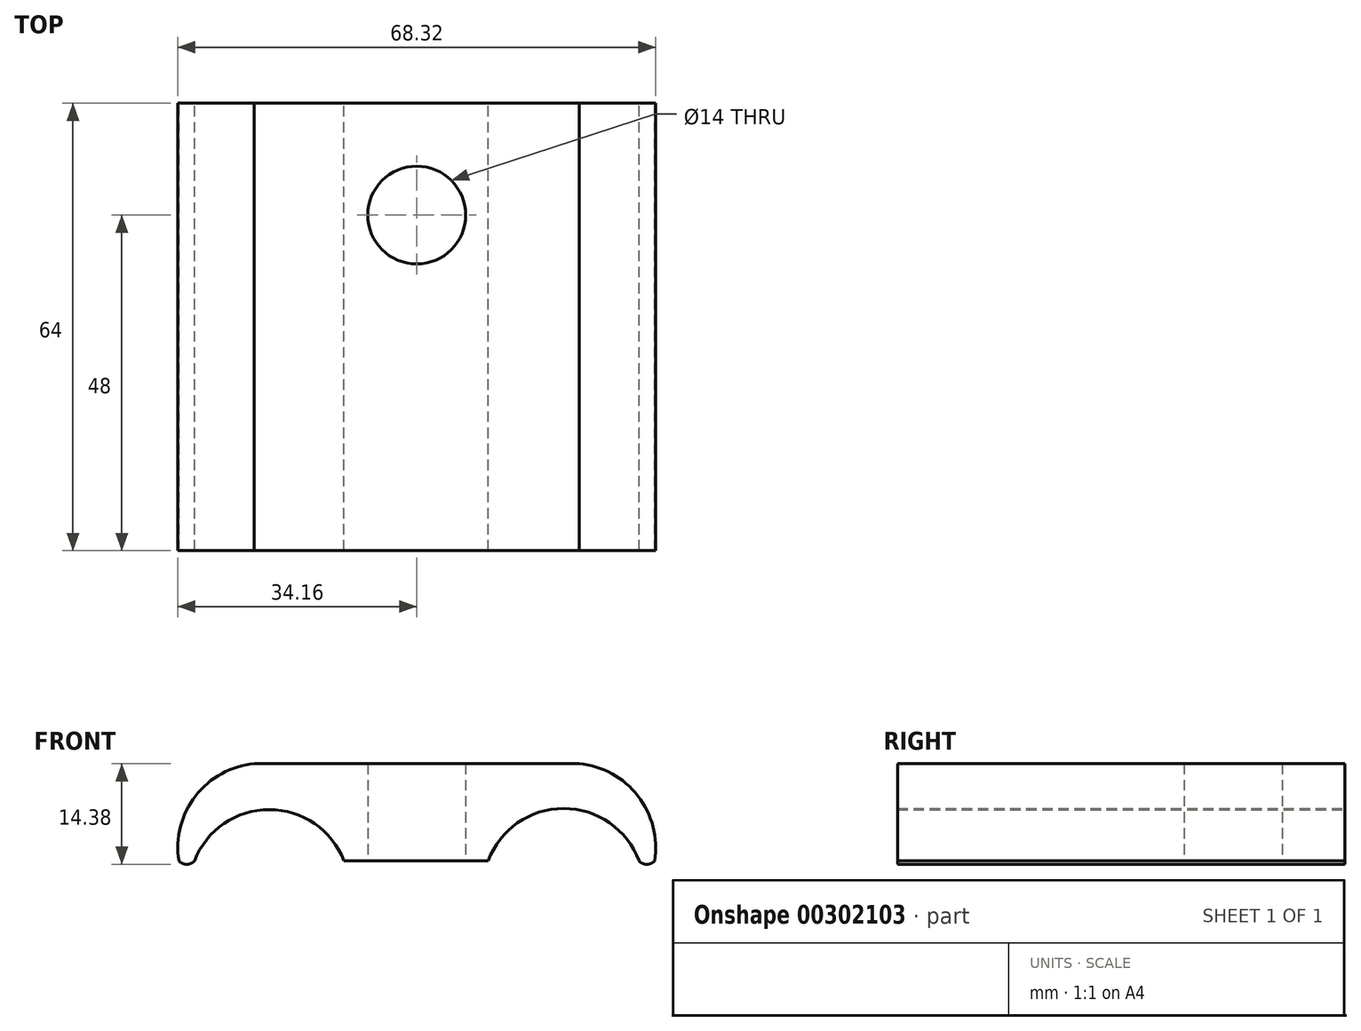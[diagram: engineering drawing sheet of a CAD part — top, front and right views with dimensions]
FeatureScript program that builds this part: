
annotation { "Feature Type Name" : "Feature", "Feature Type Description" : "" }
export const myFeature = defineFeature(function(context is Context, id is Id, definition is map)
    precondition{}
    {
        {
            var Q0;
            Q0=qCreatedBy(makeId("Front.planeOp"),FACE);
            var sketch = newSketch(context, id + "F0", { "sketchPlane" : qUnion([Q0])});
            skLineSegment(sketch, "E0", {"start": v(-34, 0) * mm, "end": v(-44.42, 0) * mm});
            skLineSegment(sketch, "E1", {"start": v(-34, 0) * mm, "end": v(-23.78, 0) * mm});
            skArc(sketch, "E2", {"start": v(-44.42, 0) * mm, "mid": v(-55.1, 7.34) * mm, "end": v(-65.78, 0) * mm});
            skArc(sketch, "E3", {"start": v(-2.22, 0) * mm, "mid": v(-13, 7.5) * mm, "end": v(-23.78, 0) * mm});
            skLineSegment(sketch, "E4", {"start": v(-13, 13.9) * mm, "end": v(-57.22, 13.9) * mm});
            skLineSegment(sketch, "E5", {"start": v(-13, 13.9) * mm, "end": v(-10.78, 13.9) * mm});
            skLineSegment(sketch, "E6", {"start": v(0, -0.1) * mm, "end": v(0, 0) * mm});
            skPoint(sketch, "E7.newPointB", {"position": v(0, 0) * mm});
            skPoint(sketch, "E8.start.orphan", {"position": v(-68, 0) * mm});
            skPoint(sketch, "E9.start.orphan", {"position": v(-65.78, 0) * mm});
            skArc(sketch, "E10", {"start": v(-55.1, 13.9) * mm, "mid": v(-64.95, 10.1) * mm, "end": v(-68, 0) * mm});
            skArc(sketch, "E11.MirrorCS", {"start": v(-12.9, 13.9) * mm, "mid": v(-4.48, 11.42) * mm, "end": v(0, 3.88) * mm});
            skPoint(sketch, "E12.orphan", {"position": v(0, 13.9) * mm});
            skPoint(sketch, "E13.orphan", {"position": v(-68, 13.9) * mm});
            skPoint(sketch, "E14.start.orphan", {"position": v(-68, 2.22) * mm});
            skArc(sketch, "E15", {"start": v(-68, 0) * mm, "mid": v(-66.9, -0.5) * mm, "end": v(-65.78, 0) * mm});
            skArc(sketch, "E16.MirrorCS", {"start": v(0, 0) * mm, "mid": v(-1.1, -0.5) * mm, "end": v(-2.22, 0) * mm});
            skArc(sketch, "E17.MirrorCS", {"start": v(-12.9, 13.9) * mm, "mid": v(-3.05, 10.1) * mm, "end": v(0, 0) * mm});
            skSolve(sketch);
        }
        {
            var Q0;
            Q0=makeQuery(id+"F0.imprint","IMPRINT",FACE,{"disambiguationData":[TD([[makeQuery(id+"F0.imprint","IMPRINT",EDGE,{"derivedFrom":sQuery(id+"F0.wireOp",EDGE,"E0")}),-1.0]])]});
            extrude(context, id + "F1", {"entities" : qUnion([Q0]), "depth" : 64 * mm});
        }
        {
            var Q0;
            Q0=qCreatedBy(makeId("Top.planeOp"),FACE);
            var sketch = newSketch(context, id + "F2", { "sketchPlane" : qUnion([Q0])});
            skLineSegment(sketch, "E18", {"start": v(0, 0) * mm, "end": v(-68, 0) * mm});
            skLineSegment(sketch, "E19", {"start": v(0, 0) * mm, "end": v(0, -64) * mm});
            skLineSegment(sketch, "E20", {"start": v(0, -32) * mm, "end": v(-34, -32) * mm});
            skPoint(sketch, "E20.endSnap0", {"position": v(-34, 0) * mm});
            skLineSegment(sketch, "E21", {"start": v(-34, -32) * mm, "end": v(-34, 0) * mm});
            skCircle(sketch, "E22", {"center": v(-34, -16) * mm, "radius": 7 * mm});
            skCircle(sketch, "E23.MirrorC", {"center": v(-34, -48) * mm, "radius": 7 * mm});
            skSolve(sketch);
        }
        {
            var Q0;
            Q0=makeQuery(id+"F2.imprint","IMPRINT",FACE,{"disambiguationData":[TD([[makeQuery(id+"F2.imprint","IMPRINT",EDGE,{"derivedFrom":sQuery(id+"F2.wireOp",EDGE,"E23.MirrorC")}),-1.0]])]});
            var Q1;
            {var subQ0=sQuery(id+"F2.wireOp",EDGE,"E22");var subQ1=sQuery(id+"F2.wireOp",EDGE,"E21");var subQ2=makeQuery(id+"F2.imprint","INTERSECT",VERTEX,{"disambiguationData":[OD(0.0)],"derivedFrom":[subQ1,subQ0]});Q1=makeQuery(id+"F2.imprint","IMPRINT",FACE,{"disambiguationData":[TD([[makeQuery(id+"F2.imprint","IMPRINT",EDGE,{"disambiguationData":[TD([[subQ2,-1.0]])],"derivedFrom":subQ1}),-1.0]])]});}
            var Q2;
            {var subQ0=sQuery(id+"F2.wireOp",EDGE,"E22");var subQ1=sQuery(id+"F2.wireOp",EDGE,"E21");var subQ2=makeQuery(id+"F2.imprint","INTERSECT",VERTEX,{"disambiguationData":[OD(0.0)],"derivedFrom":[subQ1,subQ0]});Q2=makeQuery(id+"F2.imprint","IMPRINT",FACE,{"disambiguationData":[TD([[makeQuery(id+"F2.imprint","IMPRINT",EDGE,{"disambiguationData":[TD([[subQ2,-1.0]])],"derivedFrom":subQ1}),1.0]])]});}
            var Q3;
            Q3=sQuery(id+"F2.wireOp",EDGE,"E23.MirrorC");
            var Q4;
            Q4=sQuery(id+"F2.wireOp",EDGE,"E22");
            extrude(context, id + "F3", {"entities" : qUnion([Q0, Q1, Q2]), "operationType" : NewBodyOperationType.REMOVE, "surfaceEntities" : qUnion([Q3, Q4]), "depth" : 14 * mm});
        }
    });
